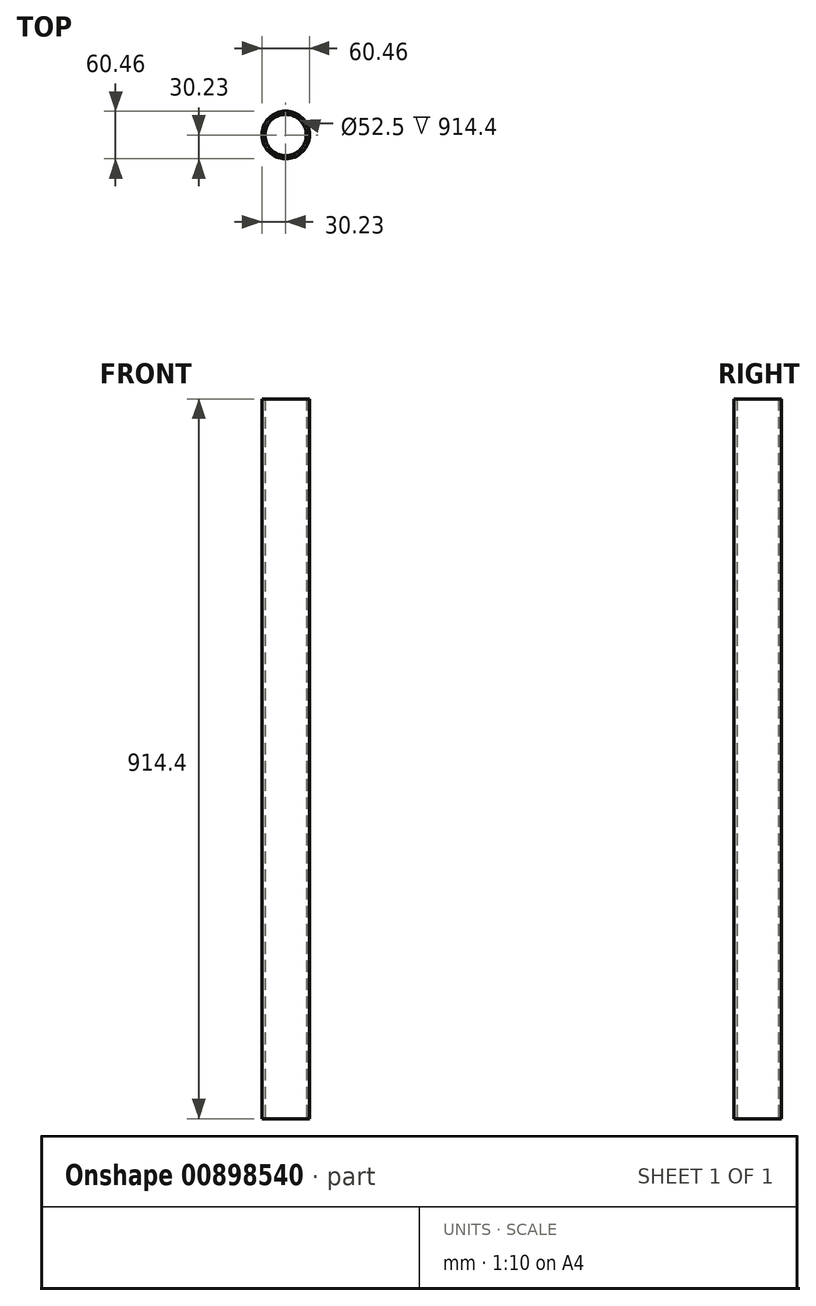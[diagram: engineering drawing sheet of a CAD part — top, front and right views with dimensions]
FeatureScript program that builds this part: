
annotation { "Feature Type Name" : "Feature", "Feature Type Description" : "" }
export const myFeature = defineFeature(function(context is Context, id is Id, definition is map)
    precondition{}
    {
        {
            var Q0;
            Q0=qCreatedBy(makeId("Top.planeOp"),FACE);
            var sketch = newSketch(context, id + "F0", { "sketchPlane" : qUnion([Q0])});
            skCircle(sketch, "E0", {"center": v(0, 0) * mm, "radius": 30.23 * mm});
            skCircle(sketch, "E1", {"center": v(0, 0) * mm, "radius": 26.25 * mm});
            skSolve(sketch);
        }
        {
            var Q0;
            Q0=makeQuery(id+"F0.imprint","IMPRINT",FACE,{"disambiguationData":[TD([[makeQuery(id+"F0.imprint","IMPRINT",EDGE,{"derivedFrom":sQuery(id+"F0.wireOp",EDGE,"E0")}),1.0]])]});
            extrude(context, id + "F1", {"entities" : qUnion([Q0]), "depth" : 914.4 * mm, "offsetDistance" : 25.4 * mm});
        }
    });
